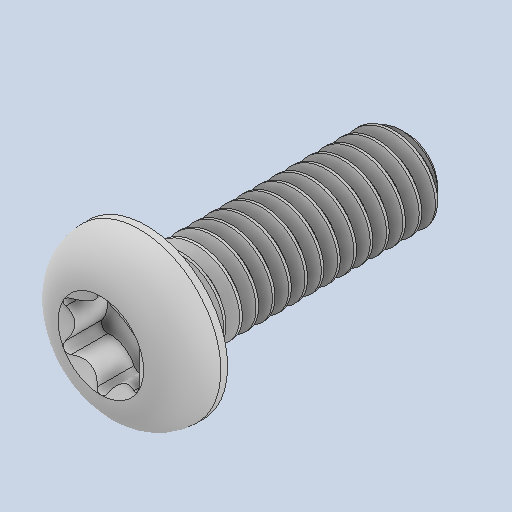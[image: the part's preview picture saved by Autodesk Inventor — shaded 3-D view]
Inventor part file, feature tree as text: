
AUTODESK INVENTOR PART (.ipt)
format: ipt  version: 2022.3 (Build 263350000, 350)  size: 694,272 bytes
history: native  units: in
note: dims shown in document units (in); Inventor stores cm internally (conversion verified against a paired STEP export)
features: extrude x1
ambient origin geometry x8: Origin, YZ Plane, XZ Plane, XY Plane, X Axis, Y Axis, Z Axis, Center Point
bodies: Solid1 (feature_tree)
feature tree (1):
  extrude  "Extrude16"  [1 undecoded]
note: 1 required parameter value undecoded (feature->parameter linkage not recoverable at this tier; creation-order binding heuristic only, values carry confidence <= 0.55)
